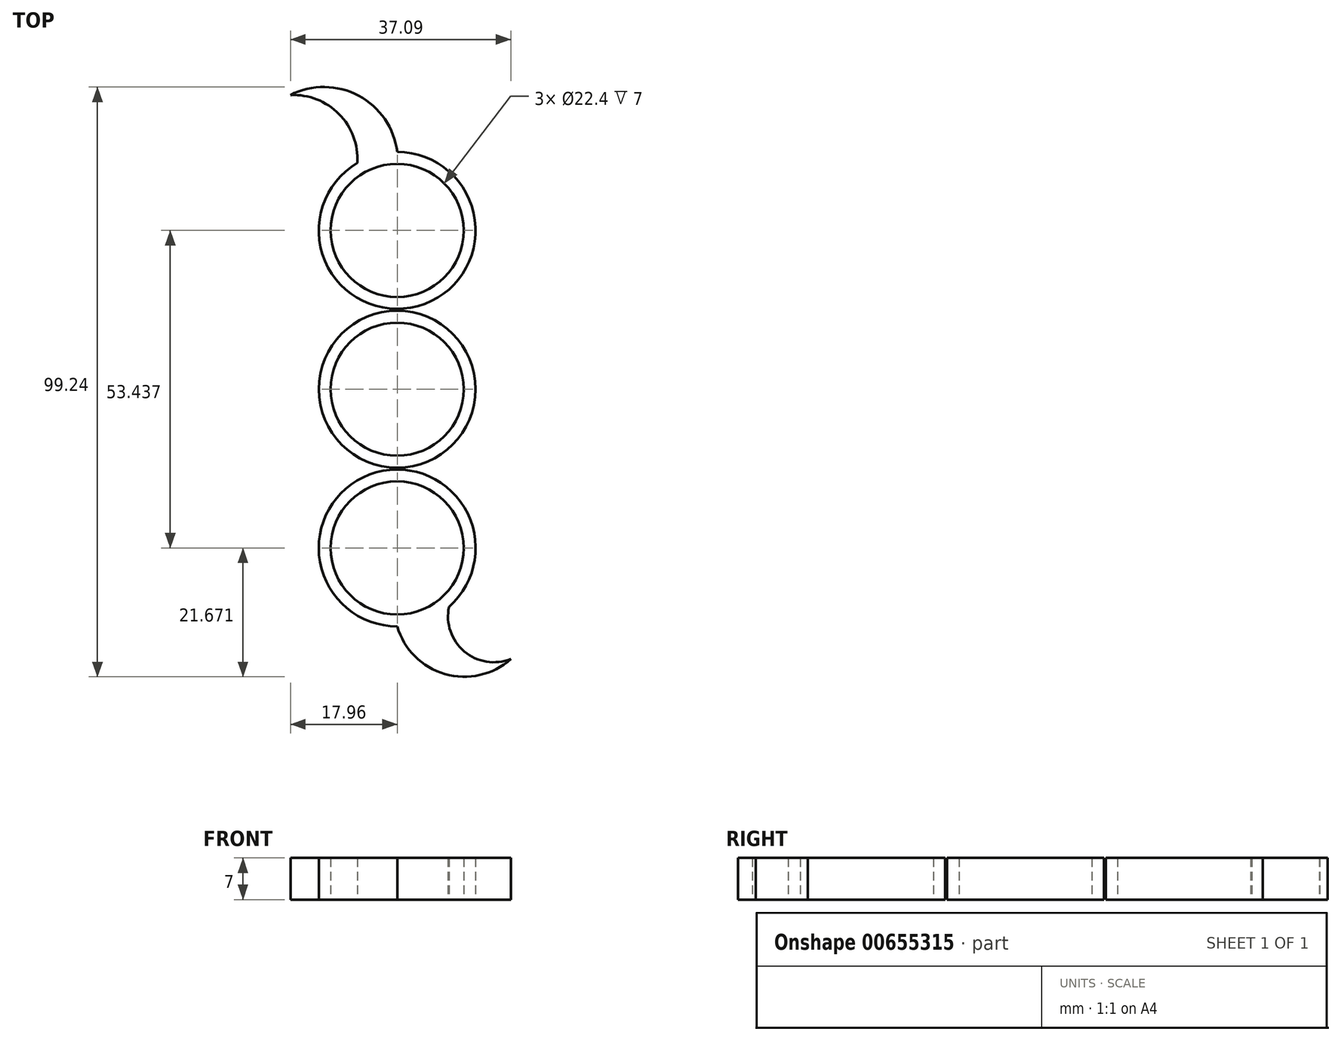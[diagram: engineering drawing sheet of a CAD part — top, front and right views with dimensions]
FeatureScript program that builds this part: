
annotation { "Feature Type Name" : "Feature", "Feature Type Description" : "" }
export const myFeature = defineFeature(function(context is Context, id is Id, definition is map)
    precondition{}
    {
        {
            var Q0;
            Q0=qCreatedBy(makeId("Top.planeOp"),FACE);
            var sketch = newSketch(context, id + "F0", { "sketchPlane" : qUnion([Q0])});
            skCircle(sketch, "E0", {"center": v(0, 0) * mm, "radius": 11.2 * mm});
            skCircle(sketch, "E1", {"center": v(0, 0) * mm, "radius": 13.2 * mm});
            skCircle(sketch, "E2", {"center": v(0, 26.72) * mm, "radius": 11.2 * mm});
            skArc(sketch, "E3", {"start": v(-6.7, 38.1) * mm, "mid": v(3.47, 13.98) * mm, "end": v(0, 39.92) * mm});
            skArc(sketch, "E4.1.0", {"start": v(8.72, -36.62) * mm, "mid": v(-4.66, -14.37) * mm, "end": v(0, -39.92) * mm});
            skCircle(sketch, "E4.1.1", {"center": v(0, -26.72) * mm, "radius": 11.2 * mm});
            skArc(sketch, "E5", {"start": v(0, 39.92) * mm, "mid": v(-6.48, 49.39) * mm, "end": v(-17.96, 49.5) * mm});
            skArc(sketch, "E6", {"start": v(-6.7, 38.1) * mm, "mid": v(-9.79, 46.3) * mm, "end": v(-17.96, 49.5) * mm});
            skArc(sketch, "E7", {"start": v(0, -39.92) * mm, "mid": v(8.05, -47.93) * mm, "end": v(19.13, -45.4) * mm});
            skArc(sketch, "E8", {"start": v(8.72, -36.62) * mm, "mid": v(11.3, -44.12) * mm, "end": v(19.13, -45.4) * mm});
            skArc(sketch, "E9", {"start": v(-13.2, 26.26) * mm, "mid": v(-18.9, 13.13) * mm, "end": v(-13.2, 0) * mm});
            skArc(sketch, "E10", {"start": v(13.12, -28.13) * mm, "mid": v(17.93, -14.08) * mm, "end": v(13.2, 0) * mm});
            skSolve(sketch);
        }
        {
            var Q0;
            Q0 = qSketchRegion(id + "F0", true);
            extrude(context, id + "F1", {"entities" : qUnion([Q0]), "depth" : 7 * mm, "offsetDistance" : 25 * mm});
        }
    });
